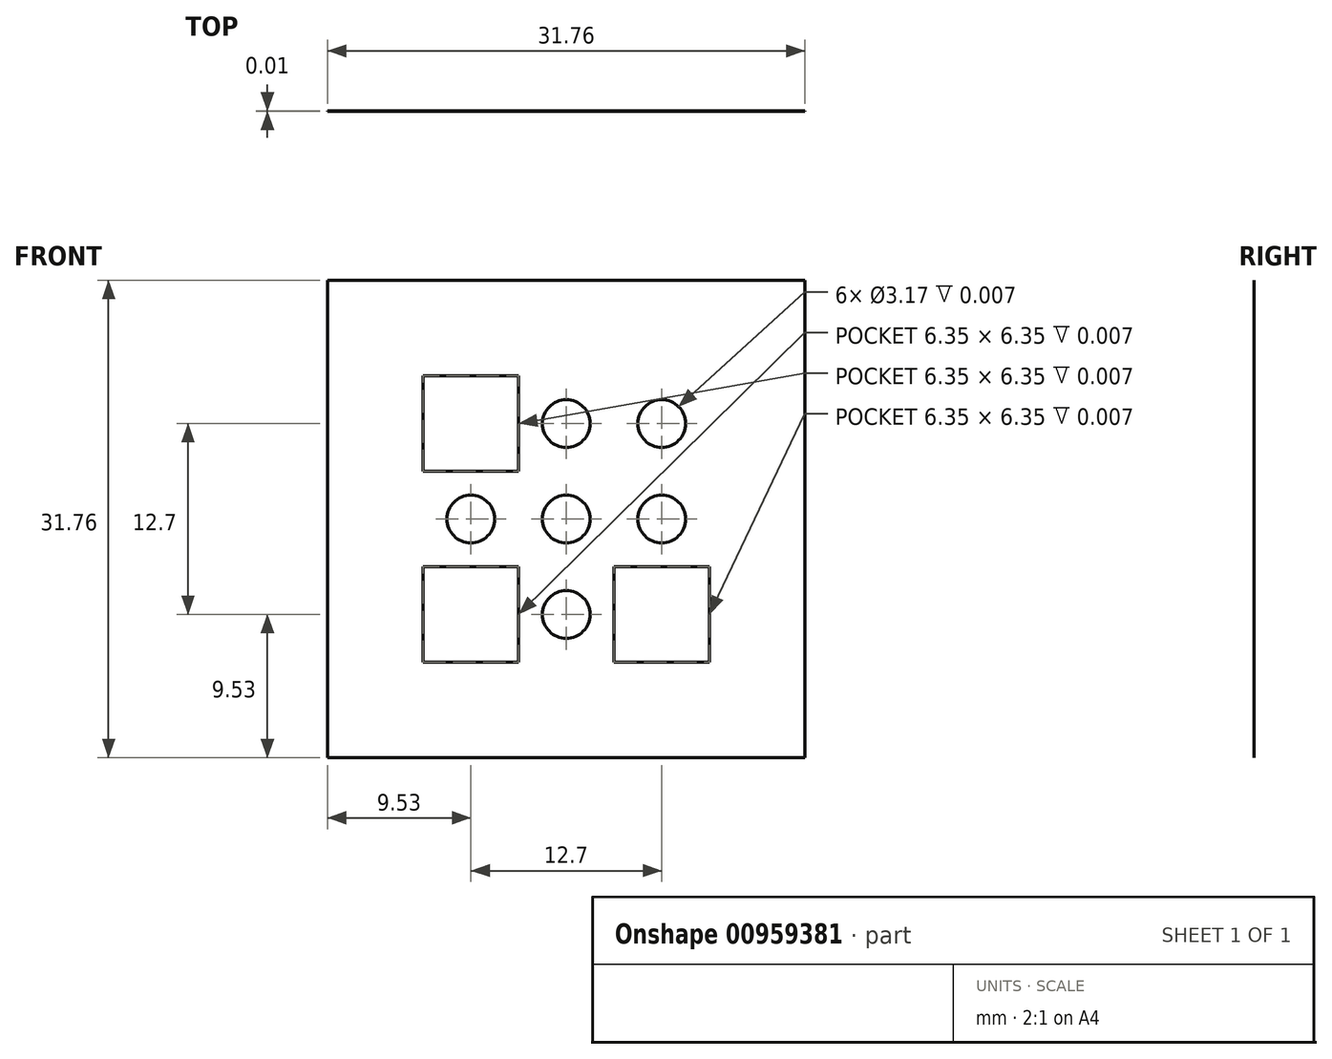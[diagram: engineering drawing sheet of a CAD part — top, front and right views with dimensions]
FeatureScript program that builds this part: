
annotation { "Feature Type Name" : "Feature", "Feature Type Description" : "" }
export const myFeature = defineFeature(function(context is Context, id is Id, definition is map)
    precondition{}
    {
        {
            var Q0;
            Q0=qCreatedBy(makeId("Front.planeOp"),FACE);
            var sketch = newSketch(context, id + "F0", { "sketchPlane" : qUnion([Q0])});
            skLineSegment(sketch, "E0.bottom", {"start": v(15.87, 15.88) * mm, "end": v(-15.88, 15.87) * mm});
            skLineSegment(sketch, "E0.top", {"start": v(15.88, -15.87) * mm, "end": v(-15.87, -15.88) * mm});
            skLineSegment(sketch, "E0.left", {"start": v(15.87, 15.88) * mm, "end": v(15.88, -15.87) * mm});
            skLineSegment(sketch, "E0.right", {"start": v(-15.88, 15.88) * mm, "end": v(-15.87, -15.88) * mm});
            skPoint(sketch, "E0.middle", {"position": v(0, 0) * mm});
            skLineSegment(sketch, "E1.bottom", {"start": v(-9.53, 9.52) * mm, "end": v(-3.18, 9.52) * mm});
            skLineSegment(sketch, "E1.top", {"start": v(-9.53, 3.17) * mm, "end": v(-3.18, 3.17) * mm});
            skLineSegment(sketch, "E1.left", {"start": v(-9.53, 9.52) * mm, "end": v(-9.53, 3.17) * mm});
            skLineSegment(sketch, "E1.right", {"start": v(-3.18, 9.52) * mm, "end": v(-3.18, 3.17) * mm});
            skLineSegment(sketch, "E2.bottom", {"start": v(-9.52, -9.53) * mm, "end": v(-3.17, -9.53) * mm});
            skLineSegment(sketch, "E2.top", {"start": v(-9.52, -3.17) * mm, "end": v(-3.17, -3.17) * mm});
            skLineSegment(sketch, "E2.left", {"start": v(-9.52, -9.53) * mm, "end": v(-9.52, -3.17) * mm});
            skLineSegment(sketch, "E2.right", {"start": v(-3.17, -9.53) * mm, "end": v(-3.17, -3.17) * mm});
            skLineSegment(sketch, "E3.bottom", {"start": v(9.52, -9.52) * mm, "end": v(3.17, -9.52) * mm});
            skLineSegment(sketch, "E3.top", {"start": v(9.52, -3.17) * mm, "end": v(3.17, -3.17) * mm});
            skLineSegment(sketch, "E3.left", {"start": v(9.52, -9.52) * mm, "end": v(9.52, -3.17) * mm});
            skLineSegment(sketch, "E3.right", {"start": v(3.17, -9.52) * mm, "end": v(3.17, -3.17) * mm});
            skCircle(sketch, "E4", {"center": v(0, -6.35) * mm, "radius": 1.59 * mm});
            skCircle(sketch, "E5", {"center": v(-6.35, 0) * mm, "radius": 1.59 * mm});
            skCircle(sketch, "E6", {"center": v(0, 0) * mm, "radius": 1.59 * mm});
            skCircle(sketch, "E7", {"center": v(0, 6.35) * mm, "radius": 1.59 * mm});
            skCircle(sketch, "E8", {"center": v(6.35, 0) * mm, "radius": 1.59 * mm});
            skCircle(sketch, "E9", {"center": v(6.35, 6.35) * mm, "radius": 1.59 * mm});
            skSolve(sketch);
        }
        {
            var Q0;
            Q0 = qSketchRegion(id + "F0", true);
            extrude(context, id + "F1", {"entities" : qUnion([Q0]), "depth" : 5 / 406.4 * mm, "offsetDistance" : 25.4 * mm});
        }
        {
            var Q0;
            Q0=makeQuery(id+"F0.imprint","IMPRINT",FACE,{"disambiguationData":[TD([[makeQuery(id+"F0.imprint","IMPRINT",EDGE,{"derivedFrom":sQuery(id+"F0.wireOp",EDGE,"E3.bottom")}),-1.0]])]});
            var Q1;
            Q1=makeQuery(id+"F0.imprint","IMPRINT",FACE,{"disambiguationData":[TD([[makeQuery(id+"F0.imprint","IMPRINT",EDGE,{"derivedFrom":sQuery(id+"F0.wireOp",EDGE,"E0.bottom")}),1.0]])]});
            var Q2;
            Q2=makeQuery(id+"F0.imprint","IMPRINT",FACE,{"disambiguationData":[TD([[makeQuery(id+"F0.imprint","IMPRINT",EDGE,{"derivedFrom":sQuery(id+"F0.wireOp",EDGE,"E2.bottom")}),1.0]])]});
            var Q3;
            Q3=makeQuery(id+"F0.imprint","IMPRINT",FACE,{"disambiguationData":[TD([[makeQuery(id+"F0.imprint","IMPRINT",EDGE,{"derivedFrom":sQuery(id+"F0.wireOp",EDGE,"E1.bottom")}),-1.0]])]});
            var Q4;
            Q4=makeQuery(id+"F0.imprint","IMPRINT",FACE,{"disambiguationData":[TD([[makeQuery(id+"F0.imprint","IMPRINT",EDGE,{"derivedFrom":sQuery(id+"F0.wireOp",EDGE,"E5")}),1.0]])]});
            var Q5;
            Q5=makeQuery(id+"F0.imprint","IMPRINT",FACE,{"disambiguationData":[TD([[makeQuery(id+"F0.imprint","IMPRINT",EDGE,{"derivedFrom":sQuery(id+"F0.wireOp",EDGE,"E6")}),1.0]])]});
            var Q6;
            Q6=makeQuery(id+"F0.imprint","IMPRINT",FACE,{"disambiguationData":[TD([[makeQuery(id+"F0.imprint","IMPRINT",EDGE,{"derivedFrom":sQuery(id+"F0.wireOp",EDGE,"E4")}),1.0]])]});
            var Q7;
            Q7=makeQuery(id+"F0.imprint","IMPRINT",FACE,{"disambiguationData":[TD([[makeQuery(id+"F0.imprint","IMPRINT",EDGE,{"derivedFrom":sQuery(id+"F0.wireOp",EDGE,"E8")}),1.0]])]});
            var Q8;
            Q8=makeQuery(id+"F0.imprint","IMPRINT",FACE,{"disambiguationData":[TD([[makeQuery(id+"F0.imprint","IMPRINT",EDGE,{"derivedFrom":sQuery(id+"F0.wireOp",EDGE,"E9")}),1.0]])]});
            var Q9;
            Q9=makeQuery(id+"F0.imprint","IMPRINT",FACE,{"disambiguationData":[TD([[makeQuery(id+"F0.imprint","IMPRINT",EDGE,{"derivedFrom":sQuery(id+"F0.wireOp",EDGE,"E7")}),1.0]])]});
            extrude(context, id + "F2", {"entities" : qUnion([Q0, Q1, Q2, Q3, Q4, Q5, Q6, Q7, Q8, Q9]), "operationType" : NewBodyOperationType.ADD, "depth" : 1 / 203.2 * mm, "offsetDistance" : 25.4 * mm});
        }
    });
